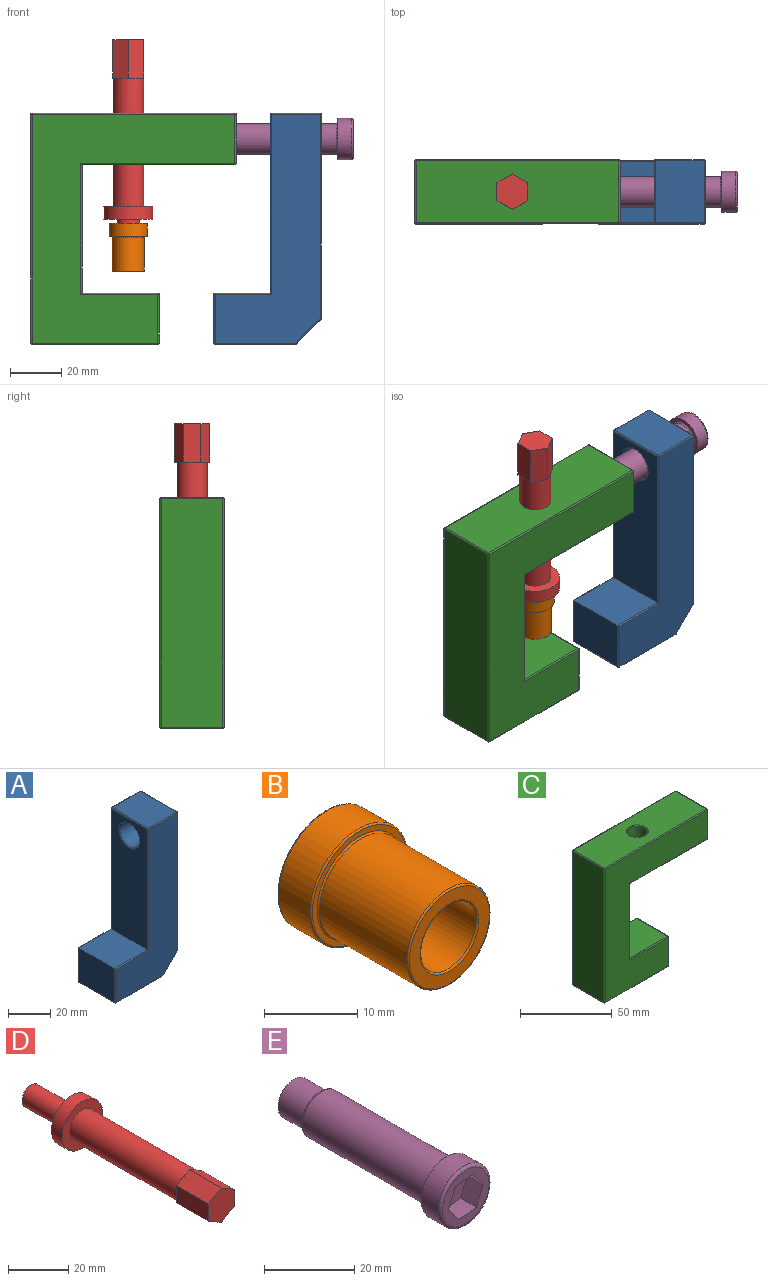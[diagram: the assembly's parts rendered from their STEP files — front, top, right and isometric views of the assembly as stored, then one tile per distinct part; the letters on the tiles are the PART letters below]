
ASSEMBLY  parts=5 mates=4
PART A: 41 faces, bbox 41.9x25x90 mm
  f0: plane 24x19.5mm, normal (-1,0,0), area 468mm2, adj f5,f15,f24,f25
  f1: plane 31.2x24mm, normal (0,0,-1), area 748.7mm2, adj f23,f24,f34,f35
  f2: plane 79.29x24mm, normal (1,0,0), area 1744.7mm2, adj f11,f27,f28,f36,f37
  f3: plane 24x19mm, normal (0,0,1), area 456mm2, adj f17,f18,f26,f27
  f4: plane 69.5x24mm, normal (-1,0,0), area 1509.6mm2, adj f5,f10,f12,f16,f17
  f5: plane 24x21.9mm, normal (0,0,1), area 525.7mm2, adj f0,f4,f13,f20
  f6: plane 89x40.9mm, normal (0,-1,0), area 2060.1mm2, adj f16,f20,f25,f26,f35,f36,f40
  f7: plane 89x40.9mm, normal (0,1,0), area 2060.1mm2, adj f12,f13,f15,f18,f23,f28,f29
  f8: plane 24x9.71mm, normal (0.71,0,-0.71), area 329.5mm2, adj f29,f34,f37,f40
  f9: cylinder r=6.6mm len=19mm, axis (1,0,0), area 787.9mm2, adj f10,f11
  f10: torus R=7.1mm, axis (-1,0,0), area 33.5mm2, adj f4,f9
  f11: torus R=7.1mm, axis (1,0,0), area 33.5mm2, adj f2,f9
  f12: cylinder r=0.5mm len=70mm, axis (0,0,-1), area 54.7mm2, adj f4,f7,f13,f14
  f13: cylinder r=0.5mm len=22.4mm, axis (-1,0,0), area 17.2mm2, adj f5,f7,f12,f15
  f14: sphere r=0.5mm, area 0.4mm2, adj f12,f17,f18
  f15: cylinder r=0.5mm len=19.5mm, axis (0,0,-1), area 15.2mm2, adj f0,f7,f13,f19
  f16: cylinder r=0.5mm len=70mm, axis (0,0,1), area 54.7mm2, adj f4,f6,f20,f21
  f17: cylinder r=0.5mm len=24mm, axis (0,-1,0), area 18.8mm2, adj f3,f4,f14,f21
  f18: cylinder r=0.5mm len=19mm, axis (-1,0,0), area 14.9mm2, adj f3,f7,f14,f22
  f19: sphere r=0.5mm, area 0.4mm2, adj f15,f23,f24
  f20: cylinder r=0.5mm len=22.4mm, axis (1,0,0), area 17.2mm2, adj f5,f6,f16,f25
  f21: sphere r=0.5mm, area 0.4mm2, adj f16,f17,f26
  f22: sphere r=0.5mm, area 0.4mm2, adj f18,f27,f28
  f23: cylinder r=0.5mm len=31.2mm, axis (1,0,0), area 24.5mm2, adj f1,f7,f19,f30
  f24: cylinder r=0.5mm len=24mm, axis (0,1,0), area 18.8mm2, adj f0,f1,f19,f31
  f25: cylinder r=0.5mm len=19.5mm, axis (0,0,1), area 15.2mm2, adj f0,f6,f20,f31
  f26: cylinder r=0.5mm len=19mm, axis (1,0,0), area 14.9mm2, adj f3,f6,f21,f32
  f27: cylinder r=0.5mm len=24mm, axis (0,-1,0), area 18.8mm2, adj f2,f3,f22,f32
  f28: cylinder r=0.5mm len=79.29mm, axis (0,0,1), area 62.3mm2, adj f2,f7,f22,f33
  f29: cylinder r=0.5mm len=10.06mm, axis (-0.71,0,-0.71), area 10.8mm2, adj f7,f8,f30,f33
  f30: sphere r=0.5mm, area 0.2mm2, adj f23,f29,f34
  f31: sphere r=0.5mm, area 0.4mm2, adj f24,f25,f35
  f32: sphere r=0.5mm, area 0.4mm2, adj f26,f27,f36
  f33: sphere r=0.5mm, area 0.2mm2, adj f28,f29,f37
  f34: cylinder r=0.5mm len=24mm, axis (0,1,0), area 9.4mm2, adj f1,f8,f30,f38
  f35: cylinder r=0.5mm len=31.2mm, axis (-1,0,0), area 24.5mm2, adj f1,f6,f31,f38
  f36: cylinder r=0.5mm len=79.29mm, axis (0,0,-1), area 62.3mm2, adj f2,f6,f32,f39
  f37: cylinder r=0.5mm len=24mm, axis (0,-1,0), area 9.4mm2, adj f2,f8,f33,f39
  f38: sphere r=0.5mm, area 0.2mm2, adj f34,f35,f40
  f39: sphere r=0.5mm, area 0.2mm2, adj f36,f37,f40
  f40: cylinder r=0.5mm len=10.06mm, axis (-0.71,0,-0.71), area 10.8mm2, adj f6,f8,f38,f39
PART B: 12 faces, bbox 16x18.7x16 mm
  f0: cylinder r=4.24mm len=18.34mm, axis (0,1,0), area 488mm2, adj f7,f9
  f1: cylinder r=7.38mm len=14.76mm, axis (0,1,0), area 219.8mm2, adj f10,f11
  f2: plane 14.36x14.36mm, normal (0,-1,0), area 30.4mm2, adj f6,f11
  f3: plane 14.36x14.36mm, normal (0,1,0), area 100.2mm2, adj f9,f10
  f4: cylinder r=6.27mm len=13.2mm, axis (0,1,0), area 520mm2, adj f6,f8
  f5: plane 12.14x12.14mm, normal (0,-1,0), area 54mm2, adj f7,f8
  f6: torus R=6.47mm, axis (0,-1,0), area 12.5mm2, adj f2,f4
  f7: torus R=4.43mm, axis (0,-1,0), area 8.5mm2, adj f0,f5
  f8: torus R=6.07mm, axis (0,-1,0), area 12.2mm2, adj f4,f5
  f9: torus R=4.43mm, axis (0,-1,0), area 8.5mm2, adj f0,f3
  f10: torus R=7.18mm, axis (0,-1,0), area 14.4mm2, adj f1,f3
  f11: torus R=7.18mm, axis (0,-1,0), area 14.4mm2, adj f1,f2
PART C: 50 faces, bbox 80x25x90 mm
  f0: plane 49x24mm, normal (0,0,-1), area 1176mm2, adj f38,f43,f46,f49
  f1: plane 24x19mm, normal (1,0,0), area 456mm2, adj f35,f44,f45,f49
  f2: plane 29.5x24mm, normal (0,0,1), area 708mm2, adj f3,f34,f35,f36
  f3: plane 50x24mm, normal (1,0,0), area 1200mm2, adj f2,f4,f30,f31
  f4: plane 59.5x24mm, normal (0,0,-1), area 1318.6mm2, adj f3,f15,f17,f25,f26
  f5: plane 24x19mm, normal (1,0,0), area 380.6mm2, adj f13,f16,f17,f18,f19
  f6: plane 79x24mm, normal (0,0,1), area 1786.6mm2, adj f14,f19,f24,f27,f28
  f7: plane 89x24mm, normal (-1,0,0), area 2136mm2, adj f28,f33,f37,f38
  f8: plane 89x79mm, normal (0,-1,0), area 3401mm2, adj f16,f24,f25,f30,f33,f34,f43,f44
  f9: plane 89x79mm, normal (0,1,0), area 3401mm2, adj f18,f26,f27,f31,f36,f37,f45,f46
  f10: cylinder r=5.4mm len=19mm, axis (0,0,-1), area 644.7mm2, adj f14,f15
  f11: cylinder r=4.4mm len=20.5mm, axis (1,0,0), area 566.7mm2, adj f12,f13
  f12: cone r=0mm half-angle=59deg, axis (1,0,0), area 71mm2, adj f11
  f13: torus R=4.9mm, axis (-1,0,0), area 22.6mm2, adj f5,f11
  f14: torus R=5.9mm, axis (0,0,-1), area 27.5mm2, adj f6,f10
  f15: torus R=5.9mm, axis (0,0,1), area 27.5mm2, adj f4,f10
  f16: cylinder r=0.5mm len=19mm, axis (0,0,-1), area 14.9mm2, adj f5,f8,f20,f21
  f17: cylinder r=0.5mm len=24mm, axis (0,1,0), area 18.8mm2, adj f4,f5,f21,f22
  f18: cylinder r=0.5mm len=19mm, axis (0,0,1), area 14.9mm2, adj f5,f9,f22,f23
  f19: cylinder r=0.5mm len=24mm, axis (0,1,0), area 18.8mm2, adj f5,f6,f20,f23
  f20: sphere r=0.5mm, area 0.4mm2, adj f16,f19,f24
  f21: sphere r=0.5mm, area 0.4mm2, adj f16,f17,f25
  f22: sphere r=0.5mm, area 0.4mm2, adj f17,f18,f26
  f23: sphere r=0.5mm, area 0.4mm2, adj f18,f19,f27
  f24: cylinder r=0.5mm len=79mm, axis (1,0,0), area 62mm2, adj f6,f8,f20,f29
  f25: cylinder r=0.5mm len=60mm, axis (-1,0,0), area 46.9mm2, adj f4,f8,f21,f30
  f26: cylinder r=0.5mm len=60mm, axis (1,0,0), area 46.9mm2, adj f4,f9,f22,f31
  f27: cylinder r=0.5mm len=79mm, axis (-1,0,0), area 62mm2, adj f6,f9,f23,f32
  f28: cylinder r=0.5mm len=24mm, axis (0,1,0), area 18.8mm2, adj f6,f7,f29,f32
  f29: sphere r=0.5mm, area 0.4mm2, adj f24,f28,f33
  f30: cylinder r=0.5mm len=51mm, axis (0,0,-1), area 39.6mm2, adj f3,f8,f25,f34
  f31: cylinder r=0.5mm len=51mm, axis (0,0,1), area 39.6mm2, adj f3,f9,f26,f36
  f32: sphere r=0.5mm, area 0.4mm2, adj f27,f28,f37
  f33: cylinder r=0.5mm len=89mm, axis (0,0,1), area 69.9mm2, adj f7,f8,f29,f39
  f34: cylinder r=0.5mm len=30mm, axis (1,0,0), area 23.3mm2, adj f2,f8,f30,f40
  f35: cylinder r=0.5mm len=24mm, axis (0,1,0), area 18.8mm2, adj f1,f2,f40,f41
  f36: cylinder r=0.5mm len=30mm, axis (-1,0,0), area 23.3mm2, adj f2,f9,f31,f41
  f37: cylinder r=0.5mm len=89mm, axis (0,0,-1), area 69.9mm2, adj f7,f9,f32,f42
  f38: cylinder r=0.5mm len=24mm, axis (0,1,0), area 18.8mm2, adj f0,f7,f39,f42
  f39: sphere r=0.5mm, area 0.4mm2, adj f33,f38,f43
  f40: sphere r=0.5mm, area 0.4mm2, adj f34,f35,f44
  f41: sphere r=0.5mm, area 0.4mm2, adj f35,f36,f45
  f42: sphere r=0.5mm, area 0.4mm2, adj f37,f38,f46
  f43: cylinder r=0.5mm len=49mm, axis (-1,0,0), area 38.5mm2, adj f0,f8,f39,f47
  f44: cylinder r=0.5mm len=19mm, axis (0,0,-1), area 14.9mm2, adj f1,f8,f40,f47
  f45: cylinder r=0.5mm len=19mm, axis (0,0,1), area 14.9mm2, adj f1,f9,f41,f48
  f46: cylinder r=0.5mm len=49mm, axis (1,0,0), area 38.5mm2, adj f0,f9,f42,f48
  f47: sphere r=0.5mm, area 0.4mm2, adj f43,f44,f49
  f48: sphere r=0.5mm, area 0.4mm2, adj f45,f46,f49
  f49: cylinder r=0.5mm len=24mm, axis (0,1,0), area 18.8mm2, adj f0,f1,f47,f48
PART D: 19 faces, bbox 19x89x19 mm
  f0: cylinder r=4.25mm len=19mm, axis (0,1,0), area 507.4mm2, adj f1,f4
  f1: plane 8.5x8.5mm, normal (0,1,0), area 56.7mm2, adj f0
  f2: cylinder r=9.5mm len=19mm, axis (0,1,0), area 298.5mm2, adj f3,f4
  f3: plane 19x19mm, normal (0,-1,0), area 170.4mm2, adj f2,f5
  f4: plane 19x19mm, normal (0,1,0), area 226.8mm2, adj f0,f2
  f5: cylinder r=6mm len=50mm, axis (0,1,0), area 1885mm2, adj f3,f6,f7,f8,f9,f10,f11
  f6: plane 5.2x3mm, normal (0,1,0), area 1.9mm2, adj f5,f12,f17
  f7: plane 6x1.73mm, normal (0,1,0), area 1.9mm2, adj f5,f12,f13
  f8: plane 5.2x3mm, normal (0,1,0), area 1.9mm2, adj f5,f13,f14
  f9: plane 5.2x3mm, normal (0,1,0), area 1.9mm2, adj f5,f14,f15
  f10: plane 6x1.73mm, normal (0,1,0), area 1.9mm2, adj f5,f15,f16
  f11: plane 5.2x3mm, normal (0,1,0), area 1.9mm2, adj f5,f16,f17
  f12: plane 15x6mm, normal (0.5,0,0.87), area 103.9mm2, adj f6,f7,f13,f17,f18
  f13: plane 15x6mm, normal (-0.5,0,0.87), area 103.9mm2, adj f7,f8,f12,f14,f18
  f14: plane 15x6.93mm, normal (-1,0,0), area 103.9mm2, adj f8,f9,f13,f15,f18
  f15: plane 15x6mm, normal (-0.5,0,-0.87), area 103.9mm2, adj f9,f10,f14,f16,f18
  f16: plane 15x6mm, normal (0.5,0,-0.87), area 103.9mm2, adj f10,f11,f15,f17,f18
  f17: plane 15x6.93mm, normal (1,0,0), area 103.9mm2, adj f6,f11,f12,f16,f18
  f18: plane 13.86x12mm, normal (0,-1,0), area 124.7mm2, adj f12,f13,f14,f15,f16,f17
PART E: 17 faces, bbox 17.3x54x17.3 mm
  f0: plane 14.6x14.6mm, normal (0,-1,0), area 88.7mm2, adj f7,f8,f9,f10,f11,f12,f14
  f1: cylinder r=5mm len=10mm, axis (0,1,0), area 251.3mm2, adj f2,f4
  f2: plane 10x10mm, normal (0,1,0), area 78.5mm2, adj f1
  f3: cylinder r=6mm len=38.6mm, axis (0,1,0), area 1455.2mm2, adj f15,f16
  f4: plane 10.6x10.6mm, normal (0,1,0), area 9.7mm2, adj f1,f15
  f5: cylinder r=8mm len=16mm, axis (0,1,0), area 266.4mm2, adj f6,f14
  f6: plane 16x16mm, normal (0,1,0), area 60mm2, adj f5,f16
  f7: plane 5x4.41mm, normal (-0.8,0,-0.6), area 27.5mm2, adj f0,f8,f12,f13
  f8: plane 5.47x5mm, normal (0.12,0,-0.99), area 27.5mm2, adj f0,f7,f9,f13
  f9: plane 5.05x5mm, normal (0.92,0,-0.4), area 27.5mm2, adj f0,f8,f10,f13
  f10: plane 5x4.41mm, normal (0.8,0,0.6), area 27.5mm2, adj f0,f9,f11,f13
  f11: plane 5.47x5mm, normal (-0.12,0,0.99), area 27.5mm2, adj f0,f10,f12,f13
  f12: plane 5.05x5mm, normal (-0.92,0,0.4), area 27.5mm2, adj f0,f7,f11,f13
  f13: plane 10.93x10.11mm, normal (0,-1,0), area 78.7mm2, adj f7,f8,f9,f10,f11,f12
  f14: torus R=7.3mm, axis (0,-1,0), area 53.5mm2, adj f0,f5
  f15: torus R=5.3mm, axis (0,-1,0), area 39.7mm2, adj f3,f4
  f16: torus R=6.7mm, axis (0,-1,0), area 43.2mm2, adj f3,f6
PLACE A t=(7.25,17.9,1.24)mm
PLACE B rot(axis=(1,0,0),90deg) t=(-26.04,5.4,28.35)mm
PLACE C t=(-14.04,17.9,1.24)mm
PLACE D rot(axis=(-1,0,0),90deg) t=(-26.04,5.4,10.95)mm
PLACE E rot(axis=(-0.58,0.58,0.58),120deg) t=(7.54,5.4,61.24)mm
MATE slider E.f1 <-> A.f9  axis (1,0,0) through (16.24,5.4,61.24)mm
MATE slider D.f0 <-> C.f10  axis (0,0,-1) through (-26.04,5.4,59.95)mm
MATE slider A.f9 <-> C.f11  axis (-1,0,0) through (29.66,5.4,61.24)mm
MATE slider B.f0 <-> D.f0  axis (0,0,1) through (-26.04,5.4,28.35)mm
